# Revit family: Bottle_Filling_Station-Elkay-EZSTLG8WSSK
name_source: partatom
category: Plumbing Fixtures
units: mm (PartAtom-declared; Revit-internal decimal feet)

## family parameters
Always vertical = Yes
Cut with Voids When Loaded = No
Maintain Annotation Orientation = No
OmniClass Number = 23.45.05.00
OmniClass Title = Sanitary Equipment
Part Type = Normal
Room Calculation Point = No
Round Connector Dimension = Use Diameter
Shared = No
Work Plane-Based = No

## types (2) — shared parameters
Activation Method = Electronic Bottle Filler Sensor with Electronic Front and Side Bubbler Pushbar
Approx. Shipping Weight (lbs) = 101
Assembly Code = D2010810
CW Connection = No
Chilling Capacity(GPH) = 8
Current = 0 A
Description = ezH2O® Bottle Filling Station & Versatile Bi-Level ADA Cooler High Efficiency Non-Filtered Refrigerated Stainless
Dimensions (L x W x H) = "36 3/4 inch x 19 inch x 39 1/16 inch"
Electrical connection distance from floor level = 17.438 "
Inlet Connection Size (inch) = 0.375 "
Installation Location = Indoor
Main Material = Finish-Elkay-Stainless Steel
Manufacturer = Elkay Manufacturer Company
Manufacturer Brand = Elkay (by Zurn Elkay Water Solutions)
Model = EZSTLG8WSSK
Mounting Type = Wall Mount (On Wall)
Number of Poles = 1
Outlet Connection Size (inch) = 1.5 "
Power Factor = 1
Product Documentation Link = https://www.elkayfiles.com
Product Installation Sheet URL = https://www.elkayfiles.com
Product Page URL = https://www.elkay.com
Product Weight (lbs) = 95
Product data URL = https://www.bimobject.com
Repair Parts URL = https://www.elkayfiles.com
URL = https://www.elkay.com
Voltage = 115 V
Waste Connection = No
Waste line = 21.875 "
Water supply = 19 "
Wrapper_Material = Finish-Elkay-Light Grey
zero-valued in all types: Default Elevation

## per-type parameters (varying)
| type | Bi-Level Water cooler | Electrical connection distance |
| EZSTLG8WSSK  Right-Hand high (Bottle Filling Station & Versatile Bi-Level ADA Cooler) | 0 " | 0 " |
| EZSTLG8WSSK  Left-Hand high (Bottle Filling Station & Versatile Bi-Level ADA Cooler) | 36.75 " | 6.625 " |

## geometry (parser evidence)
native form markers: Sweep x18
no freeform markers — native parametric forms only
